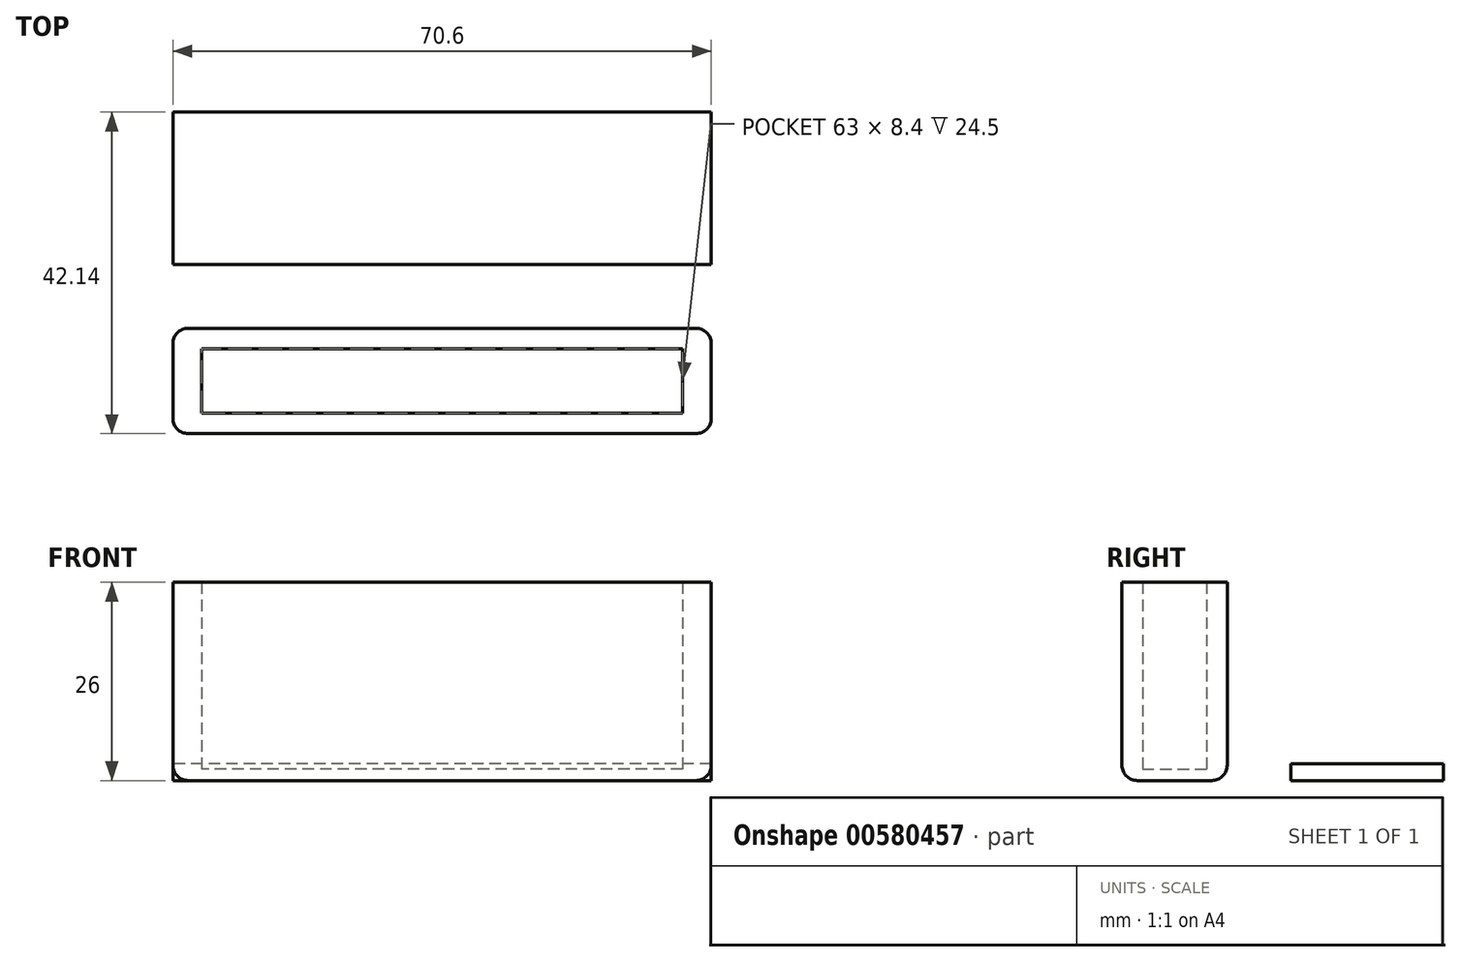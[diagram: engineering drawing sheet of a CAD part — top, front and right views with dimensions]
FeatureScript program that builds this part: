
annotation { "Feature Type Name" : "Feature", "Feature Type Description" : "" }
export const myFeature = defineFeature(function(context is Context, id is Id, definition is map)
    precondition{}
    {
        {
            var Q0;
            Q0=qCreatedBy(makeId("Top.planeOp"),FACE);
            var sketch = newSketch(context, id + "F0", { "sketchPlane" : qUnion([Q0])});
            skLineSegment(sketch, "E0.bottom", {"start": v(31.5, -4.2) * mm, "end": v(-31.5, -4.2) * mm});
            skLineSegment(sketch, "E0.top", {"start": v(31.5, 4.2) * mm, "end": v(-31.5, 4.2) * mm});
            skLineSegment(sketch, "E0.left", {"start": v(31.5, -4.2) * mm, "end": v(31.5, 4.2) * mm});
            skLineSegment(sketch, "E0.right", {"start": v(-31.5, -4.2) * mm, "end": v(-31.5, 4.2) * mm});
            skPoint(sketch, "E0.middle", {"position": v(0, 0) * mm});
            skLineSegment(sketch, "E1.0", {"start": v(-35.3, -6.9) * mm, "end": v(-35.3, 6.9) * mm});
            skLineSegment(sketch, "E1.2", {"start": v(35.3, -6.9) * mm, "end": v(35.3, 6.9) * mm});
            skLineSegment(sketch, "E2", {"start": v(-35.3, 6.9) * mm, "end": v(35.3, 6.9) * mm});
            skLineSegment(sketch, "E3", {"start": v(-35.3, -6.9) * mm, "end": v(35.3, -6.9) * mm});
            skLineSegment(sketch, "E4.bottom", {"start": v(35.3, 15.24) * mm, "end": v(-35.3, 15.24) * mm});
            skLineSegment(sketch, "E4.top", {"start": v(35.3, 35.24) * mm, "end": v(-35.3, 35.24) * mm});
            skLineSegment(sketch, "E4.left", {"start": v(35.3, 15.24) * mm, "end": v(35.3, 35.24) * mm});
            skLineSegment(sketch, "E4.right", {"start": v(-35.3, 15.24) * mm, "end": v(-35.3, 35.24) * mm});
            skPoint(sketch, "E4.middle", {"position": v(0, 25.24) * mm});
            skSolve(sketch);
        }
        {
            var Q0;
            Q0=makeQuery(id+"F0.imprint","IMPRINT",FACE,{"disambiguationData":[TD([[makeQuery(id+"F0.imprint","IMPRINT",EDGE,{"derivedFrom":sQuery(id+"F0.wireOp",EDGE,"E0.bottom")}),1.0]])]});
            extrude(context, id + "F1", {"entities" : qUnion([Q0]), "depth" : 26 * mm, "offsetDistance" : 25 * mm});
        }
        {
            var Q0;
            Q0=makeQuery(id+"F0.imprint","IMPRINT",FACE,{"disambiguationData":[TD([[makeQuery(id+"F0.imprint","IMPRINT",EDGE,{"derivedFrom":sQuery(id+"F0.wireOp",EDGE,"E0.bottom")}),-1.0]])]});
            extrude(context, id + "F2", {"entities" : qUnion([Q0]), "operationType" : NewBodyOperationType.ADD, "depth" : 1.5 * mm, "offsetDistance" : 25 * mm});
        }
        {
            var Q0;
            Q0=makeQuery(id+"F1.opExtrude","SWEPT_EDGE",EDGE,{"disambiguationData":[OSD([sQuery(id+"F0.wireOp",EDGE,"E1.0"),sQuery(id+"F0.wireOp",EDGE,"E3")])]});
            var Q1;
            Q1=makeQuery(id+"F1.opExtrude","SWEPT_EDGE",EDGE,{"disambiguationData":[OSD([sQuery(id+"F0.wireOp",EDGE,"E1.2"),sQuery(id+"F0.wireOp",EDGE,"E3")])]});
            fillet(context, id + "F3", {"entities" : qUnion([Q0, Q1]), "radius" : 2 * mm, "tangentPropagation" : true, "allowEdgeOverflow" : false});
        }
        {
            var Q0;
            Q0=makeQuery(id+"F1.opExtrude","CAP_EDGE",EDGE,{"disambiguationData":[OSD([sQuery(id+"F0.wireOp",EDGE,"E2")])],"isStart":true});
            var Q1;
            Q1=makeQuery(id+"F1.opExtrude","CAP_EDGE",EDGE,{"disambiguationData":[OSD([sQuery(id+"F0.wireOp",EDGE,"E3")])],"isStart":true});
            var Q2;
            Q2=makeQuery(id+"F1.opExtrude","SWEPT_EDGE",EDGE,{"disambiguationData":[OSD([sQuery(id+"F0.wireOp",EDGE,"E1.0"),sQuery(id+"F0.wireOp",EDGE,"E2")])]});
            var Q3;
            Q3=makeQuery(id+"F1.opExtrude","SWEPT_EDGE",EDGE,{"disambiguationData":[OSD([sQuery(id+"F0.wireOp",EDGE,"E1.2"),sQuery(id+"F0.wireOp",EDGE,"E2")])]});
            fillet(context, id + "F4", {"entities" : qUnion([Q0, Q1, Q2, Q3]), "radius" : 2 * mm, "tangentPropagation" : true, "allowEdgeOverflow" : false});
        }
        {
            var Q0;
            Q0=makeQuery(id+"F0.imprint","IMPRINT",FACE,{"disambiguationData":[TD([[makeQuery(id+"F0.imprint","IMPRINT",EDGE,{"derivedFrom":sQuery(id+"F0.wireOp",EDGE,"E4.bottom")}),-1.0]])]});
            extrude(context, id + "F5", {"entities" : qUnion([Q0]), "depth" : 2.2 * mm, "offsetDistance" : 25 * mm});
        }
    });
